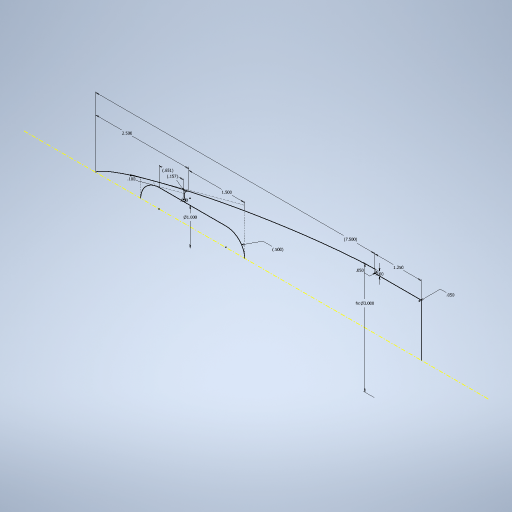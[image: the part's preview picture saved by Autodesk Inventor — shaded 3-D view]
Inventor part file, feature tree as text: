
AUTODESK INVENTOR PART (.ipt)
format: ipt  version: 2024 (Build 280153000, 153)  size: 266,240 bytes
history: native  units: in
note: dims shown in document units (in); Inventor stores cm internally (conversion verified against a paired STEP export)
features: sketch x1, other x1
ambient origin geometry x8: Origin, YZ Plane, XZ Plane, XY Plane, X Axis, Y Axis, Z Axis, Center Point
feature tree (2):
  sketch  "Sketch1"  dims[d0=0.0in d1=7.5in d2=3.0in d3=0.1in d4=1.25in d5=2.5in d6=1.0in d10=1.5in d11=7.5in d12=0.1in d14=0.05in d22=0.05in d23=0.05in d24=0.5in d25=0.157in d27=0.651in]
  other  "2D Equation Curve1"
